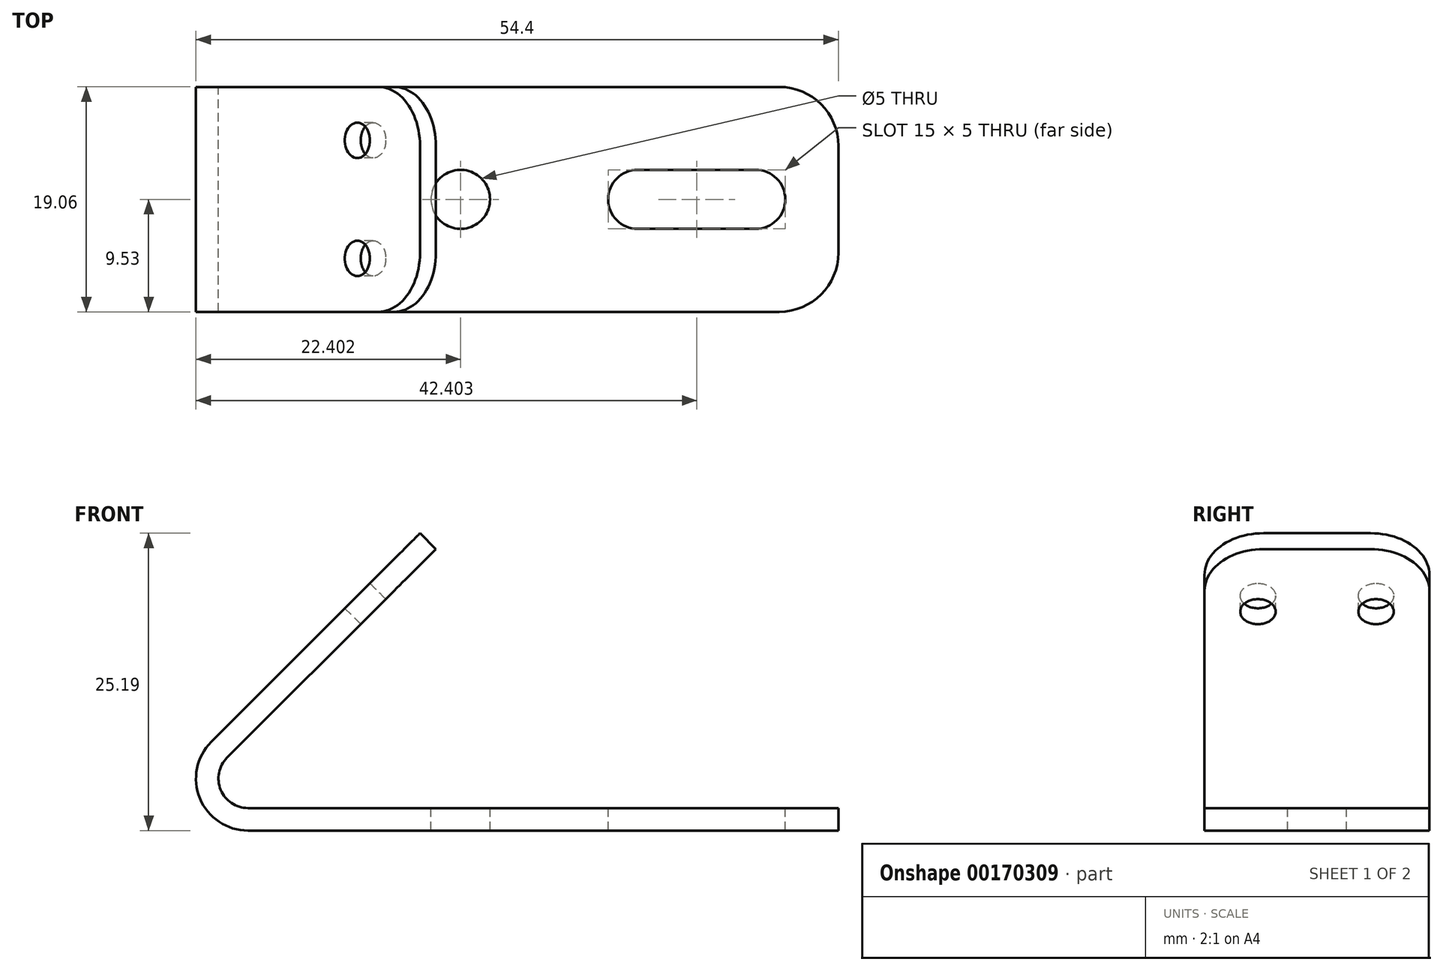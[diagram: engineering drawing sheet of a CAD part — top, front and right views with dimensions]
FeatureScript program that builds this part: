
annotation { "Feature Type Name" : "Feature", "Feature Type Description" : "" }
export const myFeature = defineFeature(function(context is Context, id is Id, definition is map)
    precondition{}
    {
        {
            var Q0;
            Q0=qCreatedBy(makeId("Front.planeOp"),FACE);
            var sketch = newSketch(context, id + "F0", { "sketchPlane" : qUnion([Q0])});
            skLineSegment(sketch, "E0", {"start": v(25.19, 25.19) * mm, "end": v(7.51, 7.51) * mm});
            skLineSegment(sketch, "E1", {"start": v(10.62, 0) * mm, "end": v(60.62, 0) * mm});
            skPoint(sketch, "E2.visualSharp", {"position": v(0, 0) * mm});
            skArc(sketch, "E2.filletArc", {"start": v(7.51, 7.51) * mm, "mid": v(6.56, 2.72) * mm, "end": v(10.62, 0) * mm});
            skLineSegment(sketch, "E3.0", {"start": v(10.62, 1.9) * mm, "end": v(60.62, 1.9) * mm});
            skArc(sketch, "E3.1", {"start": v(8.85, 6.17) * mm, "mid": v(8.31, 3.44) * mm, "end": v(10.62, 1.9) * mm});
            skLineSegment(sketch, "E3.2", {"start": v(26.53, 23.85) * mm, "end": v(8.85, 6.17) * mm});
            skLineSegment(sketch, "E4", {"start": v(25.19, 25.19) * mm, "end": v(26.53, 23.85) * mm});
            skLineSegment(sketch, "E5", {"start": v(60.62, 1.9) * mm, "end": v(60.62, 0) * mm});
            skSolve(sketch);
        }
        {
            var Q0;
            Q0 = qSketchRegion(id + "F0", true);
            extrude(context, id + "F1", {"entities" : qUnion([Q0]), "endBound" : BoundingType.SYMMETRIC, "depth" : 19.05 * mm});
        }
        {
            var Q0;
            Q0=makeQuery(id+"F1.opExtrude","CAP_EDGE",EDGE,{"disambiguationData":[OSD([sQuery(id+"F0.wireOp",EDGE,"E4")])],"isStart":false});
            var Q1;
            Q1=makeQuery(id+"F1.opExtrude","CAP_EDGE",EDGE,{"disambiguationData":[OSD([sQuery(id+"F0.wireOp",EDGE,"E4")])],"isStart":true});
            var Q2;
            Q2=makeQuery(id+"F1.opExtrude","CAP_EDGE",EDGE,{"disambiguationData":[OSD([sQuery(id+"F0.wireOp",EDGE,"E5")])],"isStart":true});
            var Q3;
            Q3=makeQuery(id+"F1.opExtrude","CAP_EDGE",EDGE,{"disambiguationData":[OSD([sQuery(id+"F0.wireOp",EDGE,"E5")])],"isStart":false});
            fillet(context, id + "F2", {"entities" : qUnion([Q0, Q1, Q2, Q3]), "radius" : 5 * mm, "tangentPropagation" : true, "allowEdgeOverflow" : false});
        }
        {
            var Q0;
            Q0=makeQuery(id+"F1.opExtrude","SWEPT_FACE",FACE,{"disambiguationData":[OSD([sQuery(id+"F0.wireOp",EDGE,"E0")])]});
            var sketch = newSketch(context, id + "F3", { "sketchPlane" : qUnion([Q0])});
            skLineSegment(sketch, "E6.top", {"start": v(5, 28.12) * mm, "end": v(-5, 28.12) * mm, "construction": true});
            skPoint(sketch, "E6.middle", {"position": v(0, 0) * mm});
            skCircle(sketch, "E7", {"center": v(-5, 28.12) * mm, "radius": 1.5 * mm});
            skCircle(sketch, "E8", {"center": v(5, 28.12) * mm, "radius": 1.5 * mm});
            skLineSegment(sketch, "E9", {"start": v(0, 0) * mm, "end": v(0, 28.12) * mm, "construction": true});
            skSolve(sketch);
        }
        {
            var Q0;
            Q0 = qSketchRegion(id + "F3", true);
            extrude(context, id + "F4", {"entities" : qUnion([Q0]), "operationType" : NewBodyOperationType.REMOVE, "endBound" : BoundingType.UP_TO_NEXT, "oppositeDirection" : true, "depth" : 25.4 * mm});
        }
        {
            var Q0;
            Q0=makeQuery(id+"F1.opExtrude","SWEPT_FACE",FACE,{"disambiguationData":[OSD([sQuery(id+"F0.wireOp",EDGE,"E3.0")])]});
            var sketch = newSketch(context, id + "F5", { "sketchPlane" : qUnion([Q0])});
            skCircle(sketch, "E10", {"center": v(28.62, 0) * mm, "radius": 2.5 * mm});
            skLineSegment(sketch, "E11", {"start": v(43.62, 0) * mm, "end": v(53.62, 0) * mm});
            skArc(sketch, "E12.0.startCap", {"start": v(43.62, -2.5) * mm, "mid": v(41.12, 0) * mm, "end": v(43.62, 2.5) * mm});
            skArc(sketch, "E12.0.endCap", {"start": v(53.62, 2.5) * mm, "mid": v(56.12, 0) * mm, "end": v(53.62, -2.5) * mm});
            skLineSegment(sketch, "E12.0.left", {"start": v(43.62, 2.5) * mm, "end": v(53.62, 2.5) * mm});
            skLineSegment(sketch, "E12.0.right", {"start": v(43.62, -2.5) * mm, "end": v(53.62, -2.5) * mm});
            skSolve(sketch);
        }
        {
            var Q0;
            Q0 = qSketchRegion(id + "F5", true);
            extrude(context, id + "F6", {"entities" : qUnion([Q0]), "operationType" : NewBodyOperationType.REMOVE, "endBound" : BoundingType.THROUGH_ALL, "oppositeDirection" : true, "depth" : 25.4 * mm});
        }
    });
